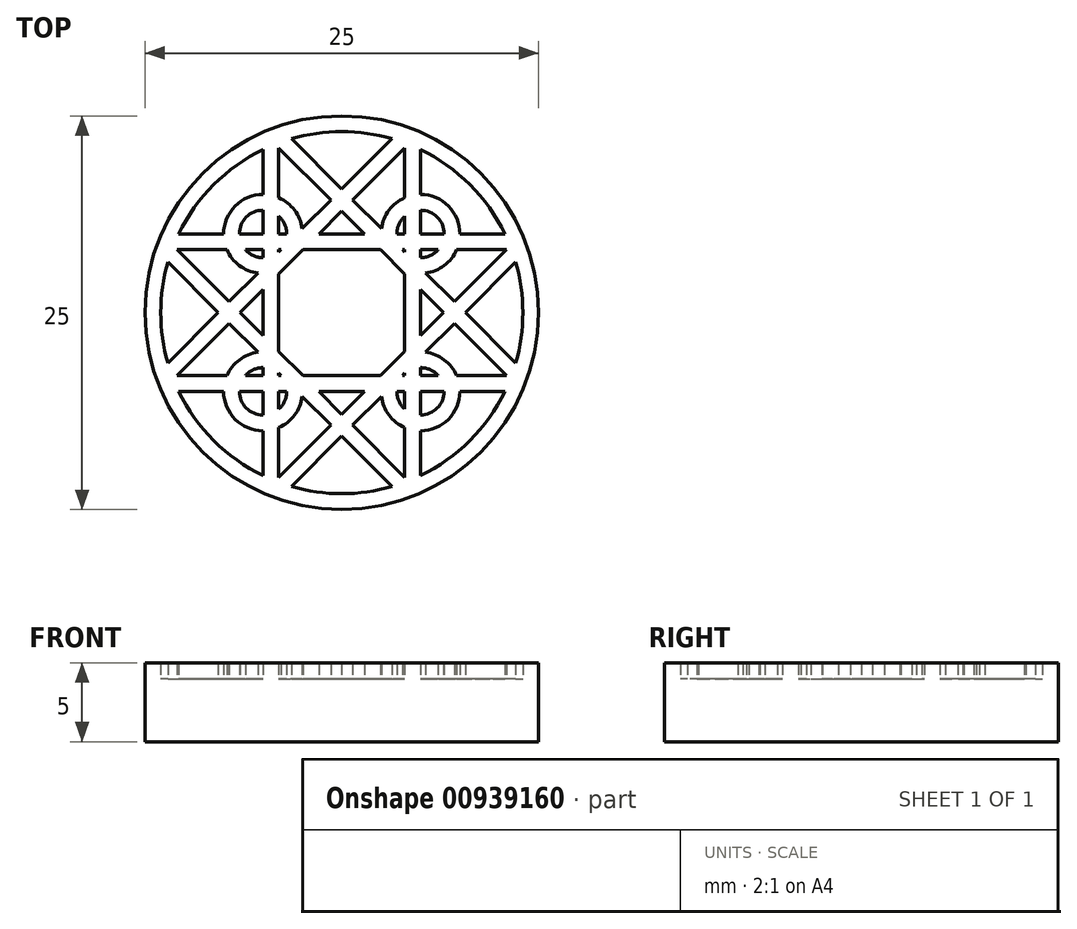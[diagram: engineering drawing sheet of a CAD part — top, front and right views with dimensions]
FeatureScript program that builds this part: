
annotation { "Feature Type Name" : "Feature", "Feature Type Description" : "" }
export const myFeature = defineFeature(function(context is Context, id is Id, definition is map)
    precondition{}
    {
        {
            var Q0;
            Q0=qCreatedBy(makeId("Top.planeOp"),FACE);
            var sketch = newSketch(context, id + "F0", { "sketchPlane" : qUnion([Q0])});
            skCircle(sketch, "E0", {"center": v(0, 0) * mm, "radius": 12.5 * mm});
            skLineSegment(sketch, "E1", {"start": v(0, 0) * mm, "end": v(-4, 0) * mm, "construction": true});
            skLineSegment(sketch, "E2", {"start": v(0, 0) * mm, "end": v(4, 0) * mm, "construction": true});
            skLineSegment(sketch, "E3", {"start": v(0, 0) * mm, "end": v(0, 4) * mm, "construction": true});
            skLineSegment(sketch, "E4", {"start": v(0, 0) * mm, "end": v(0, -4) * mm, "construction": true});
            skLineSegment(sketch, "E5", {"start": v(-4, 0) * mm, "end": v(-4, 2.46) * mm, "construction": true});
            skLineSegment(sketch, "E6", {"start": v(4, 0) * mm, "end": v(4, 2.46) * mm, "construction": true});
            skLineSegment(sketch, "E7", {"start": v(4, 0) * mm, "end": v(4, -2.46) * mm, "construction": true});
            skLineSegment(sketch, "E8", {"start": v(-4, 0) * mm, "end": v(-4, -2.46) * mm, "construction": true});
            skLineSegment(sketch, "E9", {"start": v(0, 4) * mm, "end": v(2.46, 4) * mm, "construction": true});
            skLineSegment(sketch, "E10", {"start": v(0, 4) * mm, "end": v(-2.46, 4) * mm, "construction": true});
            skLineSegment(sketch, "E11", {"start": v(0, -4) * mm, "end": v(-2.46, -4) * mm, "construction": true});
            skLineSegment(sketch, "E12", {"start": v(0, -4) * mm, "end": v(2.46, -4) * mm, "construction": true});
            skLineSegment(sketch, "E13", {"start": v(-4, 10.46) * mm, "end": v(-4, 7.3) * mm});
            skLineSegment(sketch, "E14", {"start": v(4, 10.46) * mm, "end": v(4, 7.3) * mm});
            skLineSegment(sketch, "E15", {"start": v(-10.46, -4) * mm, "end": v(-7.3, -4) * mm});
            skLineSegment(sketch, "E16", {"start": v(10.46, 4) * mm, "end": v(7.3, 4) * mm});
            skLineSegment(sketch, "E17", {"start": v(-4, 0) * mm, "end": v(-5, 0) * mm, "construction": true});
            skLineSegment(sketch, "E18", {"start": v(-5, 0) * mm, "end": v(-5, 1.46) * mm, "construction": true});
            skLineSegment(sketch, "E19", {"start": v(-5, 10.36) * mm, "end": v(-5, 7.5) * mm});
            skLineSegment(sketch, "E20", {"start": v(4, 0) * mm, "end": v(5, 0) * mm, "construction": true});
            skLineSegment(sketch, "E21", {"start": v(0, 4) * mm, "end": v(0, 5) * mm, "construction": true});
            skLineSegment(sketch, "E22", {"start": v(0, -4) * mm, "end": v(0, -5) * mm, "construction": true});
            skLineSegment(sketch, "E23", {"start": v(0, 5) * mm, "end": v(1.46, 5) * mm});
            skLineSegment(sketch, "E24", {"start": v(0, 5) * mm, "end": v(-1.46, 5) * mm});
            skLineSegment(sketch, "E25", {"start": v(0, -5) * mm, "end": v(1.46, -5) * mm});
            skLineSegment(sketch, "E26", {"start": v(0, -5) * mm, "end": v(-1.46, -5) * mm});
            skLineSegment(sketch, "E27", {"start": v(5, 0) * mm, "end": v(5, -1.46) * mm});
            skLineSegment(sketch, "E28", {"start": v(5, 0) * mm, "end": v(5, 1.46) * mm});
            skLineSegment(sketch, "E29", {"start": v(-11.05, -3.2) * mm, "end": v(-7.84, 0) * mm});
            skLineSegment(sketch, "E30", {"start": v(-10.46, -4) * mm, "end": v(-7.15, -0.7) * mm});
            skLineSegment(sketch, "E31", {"start": v(-3.2, 11.05) * mm, "end": v(0, 7.84) * mm});
            skLineSegment(sketch, "E32", {"start": v(10.46, -4) * mm, "end": v(7.15, -0.7) * mm});
            skLineSegment(sketch, "E33", {"start": v(11.05, 3.2) * mm, "end": v(7.84, 0) * mm});
            skLineSegment(sketch, "E34", {"start": v(-4, -10.46) * mm, "end": v(-0.7, -7.15) * mm});
            skLineSegment(sketch, "E35", {"start": v(4, -10.46) * mm, "end": v(0.7, -7.15) * mm});
            skLineSegment(sketch, "E36", {"start": v(-11.05, 3.2) * mm, "end": v(-7.84, 0) * mm});
            skLineSegment(sketch, "E37.trimOffspring", {"start": v(0.7, 7.15) * mm, "end": v(2.52, 5.33) * mm});
            skLineSegment(sketch, "E38.trimOffspring", {"start": v(0, 7.84) * mm, "end": v(3.2, 11.05) * mm});
            skLineSegment(sketch, "E39.trimOffspring", {"start": v(-0.7, 7.15) * mm, "end": v(-4, 10.46) * mm});
            skLineSegment(sketch, "E40.trimOffspring", {"start": v(0.7, 7.15) * mm, "end": v(4, 10.46) * mm});
            skLineSegment(sketch, "E41.trimOffspring", {"start": v(-3.5, 5) * mm, "end": v(-4, 5) * mm});
            skLineSegment(sketch, "E42.trimOffspring", {"start": v(-3.84, 4) * mm, "end": v(-4, 4) * mm, "construction": true});
            skLineSegment(sketch, "E43.trimOffspring", {"start": v(-3.84, 4) * mm, "end": v(-4, 4) * mm});
            skLineSegment(sketch, "E44.trimOffspring", {"start": v(-1.46, 5) * mm, "end": v(0, 6.46) * mm});
            skLineSegment(sketch, "E45.trimOffspring", {"start": v(-2.52, 5.33) * mm, "end": v(-0.7, 7.15) * mm});
            skLineSegment(sketch, "E46.trimOffspring", {"start": v(-4, 5) * mm, "end": v(-4, 6.13) * mm, "construction": true});
            skLineSegment(sketch, "E47.trimOffspring", {"start": v(-5, 5) * mm, "end": v(-5, 6.5) * mm, "construction": true});
            skLineSegment(sketch, "E48.trimOffspring", {"start": v(-5, 4) * mm, "end": v(-5, 3.5) * mm});
            skLineSegment(sketch, "E49.trimOffspring", {"start": v(-4, 4) * mm, "end": v(-4, 3.84) * mm});
            skLineSegment(sketch, "E50.trimOffspring", {"start": v(-5, 5) * mm, "end": v(-6.5, 5) * mm});
            skLineSegment(sketch, "E51.trimOffspring", {"start": v(-5, 4) * mm, "end": v(-6.13, 4) * mm, "construction": true});
            skLineSegment(sketch, "E52.trimOffspring", {"start": v(-5, 4) * mm, "end": v(-6.13, 4) * mm});
            skLineSegment(sketch, "E53.trimOffspring", {"start": v(-4, 3.84) * mm, "end": v(-3.84, 4) * mm});
            skLineSegment(sketch, "E54.trimOffspring", {"start": v(-4, 2.46) * mm, "end": v(-2.46, 4) * mm});
            skLineSegment(sketch, "E55.trimOffspring", {"start": v(-4, 3.84) * mm, "end": v(-4, 4) * mm, "construction": true});
            skLineSegment(sketch, "E56.trimOffspring", {"start": v(-4, 2.46) * mm, "end": v(-4, -2.46) * mm});
            skLineSegment(sketch, "E57.trimOffspring", {"start": v(-5, 3.5) * mm, "end": v(-5, 4) * mm, "construction": true});
            skLineSegment(sketch, "E58.trimOffspring", {"start": v(-5, 1.46) * mm, "end": v(-5, -1.46) * mm});
            skLineSegment(sketch, "E59.trimOffspring", {"start": v(-7.15, 0.7) * mm, "end": v(-10.46, 4) * mm});
            skLineSegment(sketch, "E60.trimOffspring", {"start": v(-7.15, 0.7) * mm, "end": v(-5.33, 2.52) * mm});
            skLineSegment(sketch, "E61.trimOffspring", {"start": v(-7.15, -0.7) * mm, "end": v(-5.33, -2.52) * mm});
            skLineSegment(sketch, "E62.trimOffspring", {"start": v(-6.46, 0) * mm, "end": v(-5, 1.46) * mm});
            skLineSegment(sketch, "E63.trimOffspring", {"start": v(5, 5) * mm, "end": v(6.5, 5) * mm});
            skLineSegment(sketch, "E64.trimOffspring", {"start": v(5, 4) * mm, "end": v(6.13, 4) * mm, "construction": true});
            skLineSegment(sketch, "E65.trimOffspring", {"start": v(4, 4) * mm, "end": v(3.84, 4) * mm});
            skLineSegment(sketch, "E66.trimOffspring", {"start": v(4, 5) * mm, "end": v(4, 6.13) * mm, "construction": true});
            skLineSegment(sketch, "E67.trimOffspring", {"start": v(5, 5) * mm, "end": v(5, 6.5) * mm});
            skLineSegment(sketch, "E68.trimOffspring", {"start": v(4, 4) * mm, "end": v(4, 3.84) * mm});
            skLineSegment(sketch, "E69.trimOffspring", {"start": v(3.84, 4) * mm, "end": v(4, 3.84) * mm});
            skLineSegment(sketch, "E70.trimOffspring", {"start": v(1.46, 5) * mm, "end": v(0, 6.46) * mm});
            skLineSegment(sketch, "E71.trimOffspring", {"start": v(3.5, 5) * mm, "end": v(4, 5) * mm});
            skLineSegment(sketch, "E72.trimOffspring", {"start": v(3.84, 4) * mm, "end": v(4, 4) * mm, "construction": true});
            skLineSegment(sketch, "E73.trimOffspring", {"start": v(2.46, 4) * mm, "end": v(-2.46, 4) * mm});
            skLineSegment(sketch, "E74.trimOffspring", {"start": v(4, 3.84) * mm, "end": v(4, 4) * mm, "construction": true});
            skLineSegment(sketch, "E75.trimOffspring", {"start": v(4, 2.46) * mm, "end": v(4, -2.46) * mm});
            skLineSegment(sketch, "E76.trimOffspring", {"start": v(5.33, 2.52) * mm, "end": v(7.15, 0.7) * mm});
            skLineSegment(sketch, "E77.trimOffspring", {"start": v(4, 2.46) * mm, "end": v(2.46, 4) * mm});
            skLineSegment(sketch, "E78.trimOffspring", {"start": v(5, 3.5) * mm, "end": v(5, 4) * mm});
            skLineSegment(sketch, "E79.trimOffspring", {"start": v(-4, -5) * mm, "end": v(-4, -6.13) * mm, "construction": true});
            skLineSegment(sketch, "E80.trimOffspring", {"start": v(-5, -5) * mm, "end": v(-5, -6.5) * mm});
            skLineSegment(sketch, "E81.trimOffspring", {"start": v(-4, -5) * mm, "end": v(-4, -6.13) * mm});
            skLineSegment(sketch, "E82.trimOffspring", {"start": v(-5, -4) * mm, "end": v(-6.13, -4) * mm, "construction": true});
            skLineSegment(sketch, "E83.trimOffspring", {"start": v(-5, -5) * mm, "end": v(-6.5, -5) * mm});
            skLineSegment(sketch, "E84.trimOffspring", {"start": v(-4, -4) * mm, "end": v(-3.84, -4) * mm});
            skLineSegment(sketch, "E85.trimOffspring", {"start": v(-4, -3.84) * mm, "end": v(-3.84, -4) * mm});
            skLineSegment(sketch, "E86.trimOffspring", {"start": v(-5, -1.46) * mm, "end": v(-6.46, 0) * mm});
            skLineSegment(sketch, "E87.trimOffspring", {"start": v(-5, -3.5) * mm, "end": v(-5, -4) * mm});
            skLineSegment(sketch, "E88.trimOffspring", {"start": v(-4, -3.84) * mm, "end": v(-4, -4) * mm, "construction": true});
            skLineSegment(sketch, "E89.trimOffspring", {"start": v(-4, -3.84) * mm, "end": v(-4, -4) * mm});
            skLineSegment(sketch, "E90.trimOffspring", {"start": v(-3.84, -4) * mm, "end": v(-4, -4) * mm, "construction": true});
            skLineSegment(sketch, "E91.trimOffspring", {"start": v(-2.46, -4) * mm, "end": v(2.46, -4) * mm});
            skLineSegment(sketch, "E92.trimOffspring", {"start": v(-2.52, -5.33) * mm, "end": v(-0.7, -7.15) * mm});
            skLineSegment(sketch, "E93.trimOffspring", {"start": v(-2.46, -4) * mm, "end": v(-4, -2.46) * mm});
            skLineSegment(sketch, "E94.trimOffspring", {"start": v(-3.5, -5) * mm, "end": v(-4, -5) * mm});
            skLineSegment(sketch, "E95.trimOffspring", {"start": v(0, -6.46) * mm, "end": v(1.46, -5) * mm});
            skLineSegment(sketch, "E96.trimOffspring", {"start": v(0, -7.84) * mm, "end": v(-3.2, -11.05) * mm});
            skLineSegment(sketch, "E97.trimOffspring", {"start": v(0, -6.46) * mm, "end": v(-1.46, -5) * mm});
            skLineSegment(sketch, "E98.trimOffspring", {"start": v(0, -7.84) * mm, "end": v(3.2, -11.05) * mm});
            skLineSegment(sketch, "E99.trimOffspring", {"start": v(5, -5) * mm, "end": v(5, -6.5) * mm});
            skLineSegment(sketch, "E100.trimOffspring", {"start": v(5, -4) * mm, "end": v(6.13, -4) * mm, "construction": true});
            skLineSegment(sketch, "E101.trimOffspring", {"start": v(4, -5) * mm, "end": v(4, -6.13) * mm, "construction": true});
            skLineSegment(sketch, "E102.trimOffspring", {"start": v(5, -4) * mm, "end": v(6.13, -4) * mm});
            skLineSegment(sketch, "E103.trimOffspring", {"start": v(4, -5) * mm, "end": v(4, -6.13) * mm});
            skLineSegment(sketch, "E104.trimOffspring", {"start": v(2.52, -5.33) * mm, "end": v(0.7, -7.15) * mm});
            skLineSegment(sketch, "E105.trimOffspring", {"start": v(2.46, -4) * mm, "end": v(4, -2.46) * mm});
            skLineSegment(sketch, "E106.trimOffspring", {"start": v(3.84, -4) * mm, "end": v(4, -4) * mm, "construction": true});
            skLineSegment(sketch, "E107.trimOffspring", {"start": v(3.84, -4) * mm, "end": v(4, -4) * mm});
            skLineSegment(sketch, "E108.trimOffspring", {"start": v(3.5, -5) * mm, "end": v(4, -5) * mm});
            skLineSegment(sketch, "E109.trimOffspring", {"start": v(5, -5) * mm, "end": v(6.5, -5) * mm});
            skLineSegment(sketch, "E110.trimOffspring", {"start": v(4, -3.84) * mm, "end": v(3.84, -4) * mm});
            skLineSegment(sketch, "E111.trimOffspring", {"start": v(5, -1.46) * mm, "end": v(6.46, 0) * mm});
            skLineSegment(sketch, "E112.trimOffspring", {"start": v(4, -3.84) * mm, "end": v(4, -4) * mm, "construction": true});
            skLineSegment(sketch, "E113.trimOffspring", {"start": v(4, -3.84) * mm, "end": v(4, -4) * mm});
            skLineSegment(sketch, "E114.trimOffspring", {"start": v(5, -3.5) * mm, "end": v(5, -4) * mm});
            skLineSegment(sketch, "E115.trimOffspring", {"start": v(6.46, 0) * mm, "end": v(5, 1.46) * mm});
            skLineSegment(sketch, "E116.trimOffspring", {"start": v(7.84, 0) * mm, "end": v(11.05, -3.2) * mm});
            skLineSegment(sketch, "E117.trimOffspring", {"start": v(7.15, 0.7) * mm, "end": v(10.46, 4) * mm});
            skLineSegment(sketch, "E118.trimOffspring", {"start": v(7.15, -0.7) * mm, "end": v(5.33, -2.52) * mm});
            skArc(sketch, "E119", {"start": v(4, 7.3) * mm, "mid": v(3, 6.5) * mm, "end": v(2.52, 5.33) * mm});
            skArc(sketch, "E120", {"start": v(4, 6.13) * mm, "mid": v(3.63, 5.62) * mm, "end": v(3.5, 5) * mm});
            skLineSegment(sketch, "E121.trimOffspring", {"start": v(5, 7.5) * mm, "end": v(5, 10.36) * mm});
            skLineSegment(sketch, "E122.trimOffspring", {"start": v(4, 7.3) * mm, "end": v(4, 10.46) * mm, "construction": true});
            skLineSegment(sketch, "E123.trimOffspring", {"start": v(4, 6.13) * mm, "end": v(4, 5) * mm});
            skArc(sketch, "E124.trimOffspring", {"start": v(5, 3.5) * mm, "mid": v(5.62, 3.63) * mm, "end": v(6.13, 4) * mm});
            skArc(sketch, "E125.trimOffspring", {"start": v(6.5, 5) * mm, "mid": v(6.06, 6.06) * mm, "end": v(5, 6.5) * mm});
            skLineSegment(sketch, "E126.trimOffspring", {"start": v(7.5, 5) * mm, "end": v(10.36, 5) * mm});
            skArc(sketch, "E127.trimOffspring", {"start": v(7.5, 5) * mm, "mid": v(6.77, 6.77) * mm, "end": v(5, 7.5) * mm});
            skLineSegment(sketch, "E128.trimOffspring", {"start": v(7.3, 4) * mm, "end": v(10.46, 4) * mm, "construction": true});
            skArc(sketch, "E129.trimOffspring", {"start": v(5.33, 2.52) * mm, "mid": v(6.5, 3) * mm, "end": v(7.3, 4) * mm});
            skArc(sketch, "E130", {"start": v(-5, 7.5) * mm, "mid": v(-6.77, 6.77) * mm, "end": v(-7.5, 5) * mm});
            skArc(sketch, "E131", {"start": v(-5, 6.5) * mm, "mid": v(-6.06, 6.06) * mm, "end": v(-6.5, 5) * mm});
            skArc(sketch, "E132", {"start": v(-7.5, -5) * mm, "mid": v(-6.77, -6.77) * mm, "end": v(-5, -7.5) * mm});
            skArc(sketch, "E133", {"start": v(-5, -3.5) * mm, "mid": v(-5.62, -3.63) * mm, "end": v(-6.13, -4) * mm});
            skArc(sketch, "E134", {"start": v(7.3, -4) * mm, "mid": v(6.5, -3) * mm, "end": v(5.33, -2.52) * mm});
            skLineSegment(sketch, "E135.trimOffspring", {"start": v(6.13, 4) * mm, "end": v(5, 4) * mm});
            skLineSegment(sketch, "E136.trimOffspring", {"start": v(-5, 7.5) * mm, "end": v(-5, 10.36) * mm, "construction": true});
            skLineSegment(sketch, "E137.trimOffspring", {"start": v(-5, 6.5) * mm, "end": v(-5, 5) * mm});
            skLineSegment(sketch, "E138.trimOffspring", {"start": v(-4, 7.3) * mm, "end": v(-4, 10.46) * mm, "construction": true});
            skLineSegment(sketch, "E139.trimOffspring", {"start": v(-4, 6.13) * mm, "end": v(-4, 5) * mm});
            skArc(sketch, "E140.trimOffspring", {"start": v(-2.52, 5.33) * mm, "mid": v(-3, 6.5) * mm, "end": v(-4, 7.3) * mm});
            skArc(sketch, "E141.trimOffspring", {"start": v(-3.5, 5) * mm, "mid": v(-3.63, 5.62) * mm, "end": v(-4, 6.13) * mm});
            skArc(sketch, "E142.trimOffspring", {"start": v(-6.13, 4) * mm, "mid": v(-5.62, 3.63) * mm, "end": v(-5, 3.5) * mm});
            skArc(sketch, "E143.trimOffspring", {"start": v(-7.3, 4) * mm, "mid": v(-6.5, 3) * mm, "end": v(-5.33, 2.52) * mm});
            skLineSegment(sketch, "E144.trimOffspring", {"start": v(-7.5, 5) * mm, "end": v(-10.36, 5) * mm});
            skLineSegment(sketch, "E145.trimOffspring", {"start": v(-7.3, 4) * mm, "end": v(-10.46, 4) * mm, "construction": true});
            skLineSegment(sketch, "E146.trimOffspring", {"start": v(-7.3, 4) * mm, "end": v(-10.46, 4) * mm});
            skLineSegment(sketch, "E147.trimOffspring", {"start": v(-7.3, -4) * mm, "end": v(-10.46, -4) * mm, "construction": true});
            skArc(sketch, "E148.trimOffspring", {"start": v(-6.5, -5) * mm, "mid": v(-6.06, -6.06) * mm, "end": v(-5, -6.5) * mm});
            skLineSegment(sketch, "E149.trimOffspring", {"start": v(-6.13, -4) * mm, "end": v(-5, -4) * mm});
            skLineSegment(sketch, "E150.trimOffspring", {"start": v(-7.5, -5) * mm, "end": v(-10.36, -5) * mm});
            skArc(sketch, "E151.trimOffspring", {"start": v(-4, -6.13) * mm, "mid": v(-3.63, -5.62) * mm, "end": v(-3.5, -5) * mm});
            skLineSegment(sketch, "E152.trimOffspring", {"start": v(-5, -7.5) * mm, "end": v(-5, -10.36) * mm});
            skArc(sketch, "E153.trimOffspring", {"start": v(-4, -7.3) * mm, "mid": v(-3, -6.5) * mm, "end": v(-2.52, -5.33) * mm});
            skLineSegment(sketch, "E154.trimOffspring", {"start": v(-4, -7.3) * mm, "end": v(-4, -10.46) * mm, "construction": true});
            skLineSegment(sketch, "E155.trimOffspring", {"start": v(-4, -7.3) * mm, "end": v(-4, -10.46) * mm});
            skArc(sketch, "E156.trimOffspring", {"start": v(3.5, -5) * mm, "mid": v(3.63, -5.62) * mm, "end": v(4, -6.13) * mm});
            skLineSegment(sketch, "E157.trimOffspring", {"start": v(7.3, -4) * mm, "end": v(10.46, -4) * mm, "construction": true});
            skLineSegment(sketch, "E158.trimOffspring", {"start": v(7.5, -5) * mm, "end": v(10.36, -5) * mm});
            skArc(sketch, "E159.trimOffspring", {"start": v(6.13, -4) * mm, "mid": v(5.62, -3.63) * mm, "end": v(5, -3.5) * mm});
            skLineSegment(sketch, "E160.trimOffspring", {"start": v(7.3, -4) * mm, "end": v(10.46, -4) * mm});
            skArc(sketch, "E161.trimOffspring", {"start": v(5, -6.5) * mm, "mid": v(6.06, -6.06) * mm, "end": v(6.5, -5) * mm});
            skLineSegment(sketch, "E162.trimOffspring", {"start": v(4, -7.3) * mm, "end": v(4, -10.46) * mm, "construction": true});
            skArc(sketch, "E163.trimOffspring", {"start": v(5, -7.5) * mm, "mid": v(6.77, -6.77) * mm, "end": v(7.5, -5) * mm});
            skLineSegment(sketch, "E164.trimOffspring", {"start": v(5, -7.5) * mm, "end": v(5, -10.36) * mm});
            skLineSegment(sketch, "E165.trimOffspring", {"start": v(4, -7.3) * mm, "end": v(4, -10.46) * mm});
            skArc(sketch, "E166.trimOffspring", {"start": v(2.52, -5.33) * mm, "mid": v(3, -6.5) * mm, "end": v(4, -7.3) * mm});
            skArc(sketch, "E167.trimOffspring", {"start": v(-5.33, -2.52) * mm, "mid": v(-6.5, -3) * mm, "end": v(-7.3, -4) * mm});
            skArc(sketch, "E168", {"start": v(-11.05, 3.2) * mm, "mid": v(-11.5, 0) * mm, "end": v(-11.05, -3.2) * mm});
            skArc(sketch, "E169.trimOffspring", {"start": v(-10.36, -5) * mm, "mid": v(-8.13, -8.13) * mm, "end": v(-5, -10.36) * mm});
            skArc(sketch, "E170.trimOffspring", {"start": v(-3.2, -11.05) * mm, "mid": v(0, -11.5) * mm, "end": v(3.2, -11.05) * mm});
            skArc(sketch, "E171.trimOffspring", {"start": v(5, -10.36) * mm, "mid": v(8.13, -8.13) * mm, "end": v(10.36, -5) * mm});
            skArc(sketch, "E172.trimOffspring", {"start": v(11.05, -3.2) * mm, "mid": v(11.5, 0) * mm, "end": v(11.05, 3.2) * mm});
            skArc(sketch, "E173.trimOffspring", {"start": v(10.36, 5) * mm, "mid": v(8.13, 8.13) * mm, "end": v(5, 10.36) * mm});
            skArc(sketch, "E174.trimOffspring", {"start": v(3.2, 11.05) * mm, "mid": v(0, 11.5) * mm, "end": v(-3.2, 11.05) * mm});
            skArc(sketch, "E175.trimOffspring", {"start": v(-5, 10.36) * mm, "mid": v(-8.13, 8.13) * mm, "end": v(-10.36, 5) * mm});
            skSolve(sketch);
        }
        {
            var Q0;
            Q0=makeQuery(id+"F0.imprint","IMPRINT",FACE,{"disambiguationData":[TD([[makeQuery(id+"F0.imprint","IMPRINT",EDGE,{"derivedFrom":sQuery(id+"F0.wireOp",EDGE,"E0")}),1.0]])]});
            extrude(context, id + "F1", {"entities" : qUnion([Q0]), "depth" : 5 * mm, "offsetDistance" : 25 * mm});
        }
        {
            var Q0;
            Q0=makeQuery(id+"F0.imprint","IMPRINT",FACE,{"disambiguationData":[TD([[makeQuery(id+"F0.imprint","IMPRINT",EDGE,{"derivedFrom":sQuery(id+"F0.wireOp",EDGE,"E54.trimOffspring")}),-1.0]])]});
            var Q1;
            Q1=makeQuery(id+"F0.imprint","IMPRINT",FACE,{"disambiguationData":[TD([[makeQuery(id+"F0.imprint","IMPRINT",EDGE,{"derivedFrom":sQuery(id+"F0.wireOp",EDGE,"E58.trimOffspring")}),-1.0]])]});
            var Q2;
            Q2=makeQuery(id+"F0.imprint","IMPRINT",FACE,{"disambiguationData":[TD([[makeQuery(id+"F0.imprint","IMPRINT",EDGE,{"derivedFrom":sQuery(id+"F0.wireOp",EDGE,"E59.trimOffspring")}),-1.0]])]});
            var Q3;
            Q3=makeQuery(id+"F0.imprint","IMPRINT",FACE,{"disambiguationData":[TD([[makeQuery(id+"F0.imprint","IMPRINT",EDGE,{"derivedFrom":sQuery(id+"F0.wireOp",EDGE,"E29")}),1.0]])]});
            var Q4;
            Q4=makeQuery(id+"F0.imprint","IMPRINT",FACE,{"disambiguationData":[TD([[makeQuery(id+"F0.imprint","IMPRINT",EDGE,{"derivedFrom":sQuery(id+"F0.wireOp",EDGE,"E15")}),1.0]])]});
            var Q5;
            Q5=makeQuery(id+"F0.imprint","IMPRINT",FACE,{"disambiguationData":[TD([[makeQuery(id+"F0.imprint","IMPRINT",EDGE,{"derivedFrom":sQuery(id+"F0.wireOp",EDGE,"E132")}),-1.0]])]});
            var Q6;
            Q6=makeQuery(id+"F0.imprint","IMPRINT",FACE,{"disambiguationData":[TD([[makeQuery(id+"F0.imprint","IMPRINT",EDGE,{"derivedFrom":sQuery(id+"F0.wireOp",EDGE,"E34")}),1.0]])]});
            var Q7;
            Q7=makeQuery(id+"F0.imprint","IMPRINT",FACE,{"disambiguationData":[TD([[makeQuery(id+"F0.imprint","IMPRINT",EDGE,{"derivedFrom":sQuery(id+"F0.wireOp",EDGE,"E96.trimOffspring")}),1.0]])]});
            var Q8;
            Q8=makeQuery(id+"F0.imprint","IMPRINT",FACE,{"disambiguationData":[TD([[makeQuery(id+"F0.imprint","IMPRINT",EDGE,{"derivedFrom":sQuery(id+"F0.wireOp",EDGE,"E35")}),-1.0]])]});
            var Q9;
            Q9=makeQuery(id+"F0.imprint","IMPRINT",FACE,{"disambiguationData":[TD([[makeQuery(id+"F0.imprint","IMPRINT",EDGE,{"derivedFrom":sQuery(id+"F0.wireOp",EDGE,"E25")}),-1.0]])]});
            var Q10;
            Q10=makeQuery(id+"F0.imprint","IMPRINT",FACE,{"disambiguationData":[TD([[makeQuery(id+"F0.imprint","IMPRINT",EDGE,{"derivedFrom":sQuery(id+"F0.wireOp",EDGE,"E158.trimOffspring")}),-1.0]])]});
            var Q11;
            Q11=makeQuery(id+"F0.imprint","IMPRINT",FACE,{"disambiguationData":[TD([[makeQuery(id+"F0.imprint","IMPRINT",EDGE,{"derivedFrom":sQuery(id+"F0.wireOp",EDGE,"E32")}),1.0]])]});
            var Q12;
            Q12=makeQuery(id+"F0.imprint","IMPRINT",FACE,{"disambiguationData":[TD([[makeQuery(id+"F0.imprint","IMPRINT",EDGE,{"derivedFrom":sQuery(id+"F0.wireOp",EDGE,"E33")}),1.0]])]});
            var Q13;
            Q13=makeQuery(id+"F0.imprint","IMPRINT",FACE,{"disambiguationData":[TD([[makeQuery(id+"F0.imprint","IMPRINT",EDGE,{"derivedFrom":sQuery(id+"F0.wireOp",EDGE,"E16")}),1.0]])]});
            var Q14;
            Q14=makeQuery(id+"F0.imprint","IMPRINT",FACE,{"disambiguationData":[TD([[makeQuery(id+"F0.imprint","IMPRINT",EDGE,{"derivedFrom":sQuery(id+"F0.wireOp",EDGE,"E27")}),1.0]])]});
            var Q15;
            Q15=makeQuery(id+"F0.imprint","IMPRINT",FACE,{"disambiguationData":[TD([[makeQuery(id+"F0.imprint","IMPRINT",EDGE,{"derivedFrom":sQuery(id+"F0.wireOp",EDGE,"E121.trimOffspring")}),-1.0]])]});
            var Q16;
            Q16=makeQuery(id+"F0.imprint","IMPRINT",FACE,{"disambiguationData":[TD([[makeQuery(id+"F0.imprint","IMPRINT",EDGE,{"derivedFrom":sQuery(id+"F0.wireOp",EDGE,"E14")}),-1.0]])]});
            var Q17;
            Q17=makeQuery(id+"F0.imprint","IMPRINT",FACE,{"disambiguationData":[TD([[makeQuery(id+"F0.imprint","IMPRINT",EDGE,{"derivedFrom":sQuery(id+"F0.wireOp",EDGE,"E31")}),1.0]])]});
            var Q18;
            Q18=makeQuery(id+"F0.imprint","IMPRINT",FACE,{"disambiguationData":[TD([[makeQuery(id+"F0.imprint","IMPRINT",EDGE,{"derivedFrom":sQuery(id+"F0.wireOp",EDGE,"E13")}),1.0]])]});
            var Q19;
            Q19=makeQuery(id+"F0.imprint","IMPRINT",FACE,{"disambiguationData":[TD([[makeQuery(id+"F0.imprint","IMPRINT",EDGE,{"derivedFrom":sQuery(id+"F0.wireOp",EDGE,"E19")}),-1.0]])]});
            var Q20;
            Q20=makeQuery(id+"F0.imprint","IMPRINT",FACE,{"disambiguationData":[TD([[makeQuery(id+"F0.imprint","IMPRINT",EDGE,{"derivedFrom":sQuery(id+"F0.wireOp",EDGE,"E23")}),1.0]])]});
            var Q21;
            Q21=makeQuery(id+"F0.imprint","IMPRINT",FACE,{"disambiguationData":[TD([[makeQuery(id+"F0.imprint","IMPRINT",EDGE,{"derivedFrom":sQuery(id+"F0.wireOp",EDGE,"E50.trimOffspring")}),-1.0]])]});
            var Q22;
            Q22=makeQuery(id+"F0.imprint","IMPRINT",FACE,{"disambiguationData":[TD([[makeQuery(id+"F0.imprint","IMPRINT",EDGE,{"derivedFrom":sQuery(id+"F0.wireOp",EDGE,"E41.trimOffspring")}),-1.0]])]});
            var Q23;
            Q23=makeQuery(id+"F0.imprint","IMPRINT",FACE,{"disambiguationData":[TD([[makeQuery(id+"F0.imprint","IMPRINT",EDGE,{"derivedFrom":sQuery(id+"F0.wireOp",EDGE,"E48.trimOffspring")}),-1.0]])]});
            var Q24;
            Q24=makeQuery(id+"F0.imprint","IMPRINT",FACE,{"disambiguationData":[TD([[makeQuery(id+"F0.imprint","IMPRINT",EDGE,{"derivedFrom":sQuery(id+"F0.wireOp",EDGE,"E87.trimOffspring")}),-1.0]])]});
            var Q25;
            Q25=makeQuery(id+"F0.imprint","IMPRINT",FACE,{"disambiguationData":[TD([[makeQuery(id+"F0.imprint","IMPRINT",EDGE,{"derivedFrom":sQuery(id+"F0.wireOp",EDGE,"E80.trimOffspring")}),-1.0]])]});
            var Q26;
            Q26=makeQuery(id+"F0.imprint","IMPRINT",FACE,{"disambiguationData":[TD([[makeQuery(id+"F0.imprint","IMPRINT",EDGE,{"derivedFrom":sQuery(id+"F0.wireOp",EDGE,"E81.trimOffspring")}),1.0]])]});
            var Q27;
            Q27=makeQuery(id+"F0.imprint","IMPRINT",FACE,{"disambiguationData":[TD([[makeQuery(id+"F0.imprint","IMPRINT",EDGE,{"derivedFrom":sQuery(id+"F0.wireOp",EDGE,"E102.trimOffspring")}),1.0]])]});
            var Q28;
            Q28=makeQuery(id+"F0.imprint","IMPRINT",FACE,{"disambiguationData":[TD([[makeQuery(id+"F0.imprint","IMPRINT",EDGE,{"derivedFrom":sQuery(id+"F0.wireOp",EDGE,"E99.trimOffspring")}),1.0]])]});
            var Q29;
            Q29=makeQuery(id+"F0.imprint","IMPRINT",FACE,{"disambiguationData":[TD([[makeQuery(id+"F0.imprint","IMPRINT",EDGE,{"derivedFrom":sQuery(id+"F0.wireOp",EDGE,"E103.trimOffspring")}),-1.0]])]});
            var Q30;
            Q30=makeQuery(id+"F0.imprint","IMPRINT",FACE,{"disambiguationData":[TD([[makeQuery(id+"F0.imprint","IMPRINT",EDGE,{"derivedFrom":sQuery(id+"F0.wireOp",EDGE,"E78.trimOffspring")}),-1.0]])]});
            var Q31;
            Q31=makeQuery(id+"F0.imprint","IMPRINT",FACE,{"disambiguationData":[TD([[makeQuery(id+"F0.imprint","IMPRINT",EDGE,{"derivedFrom":sQuery(id+"F0.wireOp",EDGE,"E63.trimOffspring")}),1.0]])]});
            var Q32;
            Q32=makeQuery(id+"F0.imprint","IMPRINT",FACE,{"disambiguationData":[TD([[makeQuery(id+"F0.imprint","IMPRINT",EDGE,{"derivedFrom":sQuery(id+"F0.wireOp",EDGE,"E71.trimOffspring")}),1.0]])]});
            var Q33;
            Q33=makeQuery(id+"F0.imprint","IMPRINT",FACE,{"disambiguationData":[TD([[makeQuery(id+"F0.imprint","IMPRINT",EDGE,{"derivedFrom":sQuery(id+"F0.wireOp",EDGE,"E65.trimOffspring")}),1.0]])]});
            var Q34;
            Q34=makeQuery(id+"F0.imprint","IMPRINT",FACE,{"disambiguationData":[TD([[makeQuery(id+"F0.imprint","IMPRINT",EDGE,{"derivedFrom":sQuery(id+"F0.wireOp",EDGE,"E107.trimOffspring")}),1.0]])]});
            var Q35;
            Q35=makeQuery(id+"F0.imprint","IMPRINT",FACE,{"disambiguationData":[TD([[makeQuery(id+"F0.imprint","IMPRINT",EDGE,{"derivedFrom":sQuery(id+"F0.wireOp",EDGE,"E84.trimOffspring")}),1.0]])]});
            var Q36;
            Q36=makeQuery(id+"F0.imprint","IMPRINT",FACE,{"disambiguationData":[TD([[makeQuery(id+"F0.imprint","IMPRINT",EDGE,{"derivedFrom":sQuery(id+"F0.wireOp",EDGE,"E43.trimOffspring")}),1.0]])]});
            extrude(context, id + "F2", {"entities" : qUnion([Q0, Q1, Q2, Q3, Q4, Q5, Q6, Q7, Q8, Q9, Q10, Q11, Q12, Q13, Q14, Q15, Q16, Q17, Q18, Q19, Q20, Q21, Q22, Q23, Q24, Q25, Q26, Q27, Q28, Q29, Q30, Q31, Q32, Q33, Q34, Q35, Q36]), "operationType" : NewBodyOperationType.ADD, "depth" : 4 * mm, "offsetDistance" : 25 * mm});
        }
    });
